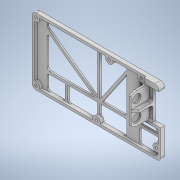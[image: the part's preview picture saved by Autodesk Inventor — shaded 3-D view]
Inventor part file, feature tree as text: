
AUTODESK INVENTOR PART (.ipt)
format: ipt  version: 2021 (Build 250183000, 183)  size: 621,056 bytes
history: native  units: mm
features: sketch x24, extrude x23, fillet x8, hole x1, chamfer x1
ambient origin geometry x8: Origin, YZ Plane, XZ Plane, XY Plane, X Axis, Y Axis, Z Axis, Center Point
bodies: Solid1 (feature_tree)
feature tree (57):
  extrude  "Extrusion1"  Depth=52.0mm
  fillet  "Fillet1"  Radius=2.0mm
  extrude  "Extrusion2"  Depth=2.0mm
  hole  "Hole1"  [1 undecoded]
  extrude  "Extrusion3"  Depth=3.0mm
  extrude  "Extrusion4"  Depth=3.0mm
  fillet  "Fillet2"  Radius=50.0mm
  fillet  "Fillet3"  Radius=8.0mm
  extrude  "Extrusion5"  Depth=3.0mm
  extrude  "Extrusion6"  Depth=49.0mm
  extrude  "Extrusion7"  Depth=49.0mm
  extrude  "Extrusion8"  Depth=6.0mm
  extrude  "Extrusion9"  Depth=6.0mm
  extrude  "Extrusion11"  Depth=6.0mm
  extrude  "Extrusion12"  Depth=24.0mm
  fillet  "Fillet6"  Radius=2.0mm
  fillet  "Fillet7"  Radius=2.0mm
  extrude  "Extrusion13"  Depth=15.0mm
  extrude  "Extrusion14"  Depth=2.0mm
  extrude  "Extrusion15"  Depth=2.0mm
  extrude  "Extrusion16"  Depth=1.2mm TaperAngle=0.0deg
  fillet  "Fillet8"  Radius=25.0mm
  extrude  "Extrusion17"  Depth=1.2mm TaperAngle=0.0deg
  extrude  "Extrusion18"  Depth=2.0mm
  extrude  "Extrusion19"  Depth=29.0mm
  extrude  "Extrusion20"  Depth=2.0mm
  extrude  "Extrusion21"  Depth=3.0mm TaperAngle=0.0deg
  extrude  "Extrusion22"  Depth=1.4mm
  fillet  "Fillet9"  Radius=3.0mm
  chamfer  "Chamfer1"  Distance=1.5mm
  fillet  "Fillet10"  Radius=3.0mm
  extrude  "Extrusion23"  Depth=1.0mm
  extrude  "Extrusion24"  Depth=3.0mm
  sketch  "Sketch1"  dims[d0=100.0mm d1=52.0mm d2=2.0mm]
  sketch  "Sketch2"  dims[d3=2.0mm d4=2.0mm]
  sketch  "Sketch3"  dims[d5=2.0mm d6=3.0mm d7=0.0mm]
  sketch  "Sketch4"  dims[d8=3.0mm d9=3.0mm]
  sketch  "Sketch5"  dims[d10=3.0mm d11=3.0mm d12=50.0mm d13=8.0mm]
  sketch  "Sketch6"  dims[d14=97.0mm d15=3.0mm]
  sketch  "Sketch7"  dims[d16=49.0mm d17=60.0mm]
  sketch  "Sketch8"  dims[d18=49.0mm d19=85.0mm]
  sketch  "Sketch9"  dims[d20=49.0mm d21=6.0mm]
  sketch  "Sketch10"  dims[d22=6.0mm d23=6.0mm]
  sketch  "Sketch12"  dims[d24=6.0mm d25=6.0mm]
  sketch  "Sketch13"  dims[d26=3.0mm d27=0.0mm]
  sketch  "Sketch14"  dims[d28=2.0mm d29=6.0mm d30=4.0mm d31=2.0mm d32=90.0deg d33=4.0mm d34=20.594885mm d35=24.0mm d36=2.0mm d37=2.0mm]
  sketch  "Sketch15"  dims[d38=15.0mm d39=15.0mm]
  sketch  "Sketch16"  dims[d40=2.0mm d41=2.0mm]
  sketch  "Sketch17"  dims[d42=2.0mm d43=2.0mm]
  sketch  "Sketch18"  dims[d44=2.0mm d45=1.2mm d46=0.0mm d47=25.0mm]
  sketch  "Sketch19"  dims[d48=2.0mm d49=1.2mm d50=0.0mm]
  sketch  "Sketch20"  dims[d51=2.0mm d52=2.0mm]
  sketch  "Sketch21"  dims[d53=12.0mm d54=29.0mm]
  sketch  "Sketch22"  dims[d55=10.0mm d56=0.0mm d57=2.0mm]
  sketch  "Sketch23"  dims[d58=2.0mm d59=3.0mm d60=0.0mm]
  sketch  "Sketch24"  dims[d62=1.4mm d63=1.4mm d64=3.0mm d65=1.5mm d66=0.0mm d67=3.0mm]
  sketch  "Sketch25"  dims[d68=1.0mm d69=1.0mm d70=3.0mm d71=2.0mm d72=0.0mm d73=3.0mm d74=1.5mm d75=0.0mm d79=10.0mm d80=18.0mm d81=1.0mm d82=1.0mm d83=3.0mm d84=1.2mm d85=0.0mm d86=41.096396mm d87=10.0mm d88=5.0mm d89=5.0mm d90=3.0mm d91=0.8mm d92=4.5mm d93=1.2mm d94=0.0mm d95=2.0mm d96=2.0mm d97=5.0mm d98=0.0mm d99=2.0mm d100=3.0mm d101=0.0mm d102=0.2mm d103=1.5mm d104=0.0mm d105=4.0mm d106=4.5mm d107=0.0mm d108=3.0mm d109=12.0mm d110=0.0mm d111=0.3mm d112=12.0mm d113=0.0mm d114=6.5mm d115=6.5mm d116=7.0mm d117=7.0mm d118=29.0mm d119=42.0mm d120=12.0mm d121=0.0mm d122=11.0mm d123=11.0mm d124=0.3mm d125=0.2mm d126=2.0mm d127=0.0mm d128=0.6mm d129=2.0mm d130=0.0mm d131=2.0mm d132=11.0mm d133=11.0mm d134=2.0mm d135=3.0mm d136=0.0mm d137=2.0mm d138=3.0mm d139=2.0mm d140=45.0deg d141=2.0mm d142=1.5mm d143=0.0mm d144=1.0mm d145=1.0mm d146=3.0mm d147=0.0mm d76=0.872665mm]
note: 1 required parameter value undecoded (feature->parameter linkage not recoverable at this tier; creation-order binding heuristic only, values carry confidence <= 0.55)
